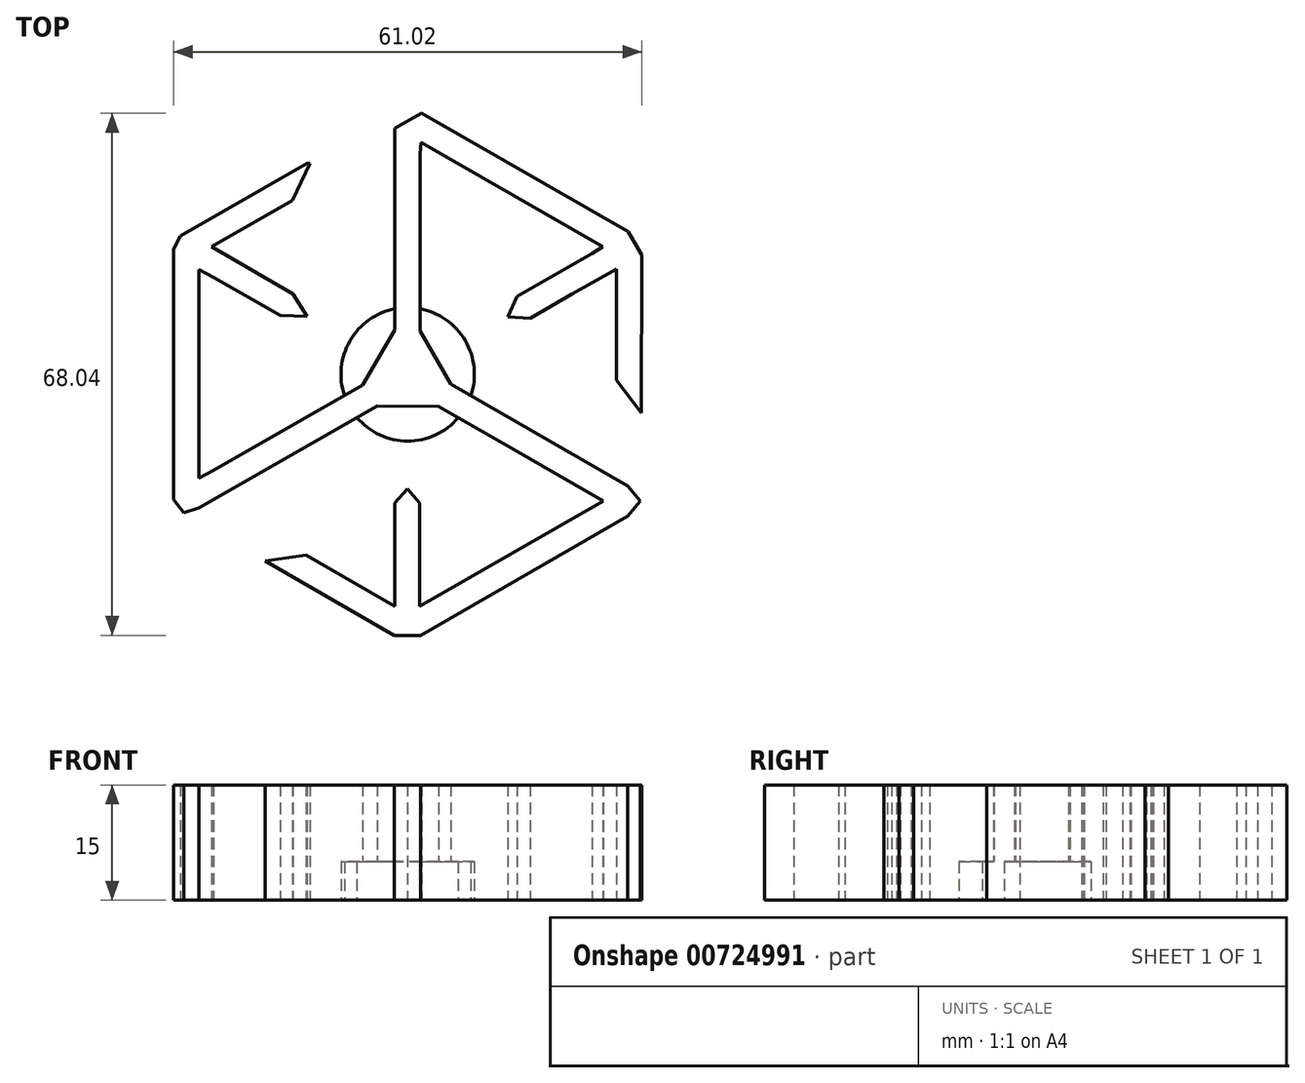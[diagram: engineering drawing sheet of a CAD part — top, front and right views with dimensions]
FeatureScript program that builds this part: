
annotation { "Feature Type Name" : "Feature", "Feature Type Description" : "" }
export const myFeature = defineFeature(function(context is Context, id is Id, definition is map)
    precondition{}
    {
        {
            var Q0;
            Q0=qCreatedBy(makeId("Top.planeOp"),FACE);
            var sketch = newSketch(context, id + "F0", { "sketchPlane" : qUnion([Q0])});
            skLineSegment(sketch, "E0", {"start": v(30.48, -5.05) * mm, "end": v(27.22, -0.75) * mm});
            skLineSegment(sketch, "E1", {"start": v(27.22, -0.75) * mm, "end": v(27.22, 13.73) * mm});
            skLineSegment(sketch, "E2", {"start": v(27.22, 13.73) * mm, "end": v(21.44, 10.46) * mm});
            skLineSegment(sketch, "E3", {"start": v(21.44, 10.46) * mm, "end": v(15.95, 7.3) * mm});
            skLineSegment(sketch, "E4", {"start": v(15.95, 7.3) * mm, "end": v(13.04, 7.5) * mm});
            skLineSegment(sketch, "E5", {"start": v(13.04, 7.5) * mm, "end": v(14.24, 10.14) * mm});
            skLineSegment(sketch, "E6", {"start": v(14.24, 10.14) * mm, "end": v(24.02, 15.76) * mm});
            skLineSegment(sketch, "E7", {"start": v(24.02, 15.76) * mm, "end": v(25.41, 16.65) * mm});
            skLineSegment(sketch, "E8", {"start": v(25.41, 16.65) * mm, "end": v(1.75, 30.23) * mm});
            skLineSegment(sketch, "E9", {"start": v(1.75, 30.23) * mm, "end": v(1.6, 28.74) * mm});
            skLineSegment(sketch, "E10", {"start": v(1.6, 28.74) * mm, "end": v(1.6, 5.63) * mm});
            skLineSegment(sketch, "E11", {"start": v(1.6, 5.63) * mm, "end": v(5.62, -1.29) * mm});
            skLineSegment(sketch, "E12", {"start": v(5.62, -1.29) * mm, "end": v(28.68, -14.56) * mm});
            skLineSegment(sketch, "E13", {"start": v(28.68, -14.56) * mm, "end": v(30.33, -16.5) * mm});
            skLineSegment(sketch, "E14", {"start": v(30.33, -16.5) * mm, "end": v(28.7, -18.47) * mm});
            skLineSegment(sketch, "E15", {"start": v(28.7, -18.47) * mm, "end": v(1.66, -34.02) * mm});
            skLineSegment(sketch, "E16", {"start": v(1.66, -34.02) * mm, "end": v(-1.74, -34.02) * mm});
            skLineSegment(sketch, "E17", {"start": v(-1.74, -34.02) * mm, "end": v(-18.56, -24.35) * mm});
            skLineSegment(sketch, "E18", {"start": v(-18.56, -24.35) * mm, "end": v(-13.27, -23.57) * mm});
            skLineSegment(sketch, "E19", {"start": v(-13.27, -23.57) * mm, "end": v(-1.67, -30.21) * mm});
            skLineSegment(sketch, "E20", {"start": v(-1.67, -30.21) * mm, "end": v(-1.67, -25.25) * mm});
            skLineSegment(sketch, "E21", {"start": v(-1.67, -25.25) * mm, "end": v(-1.66, -16.78) * mm});
            skLineSegment(sketch, "E22", {"start": v(-1.66, -16.78) * mm, "end": v(-0.03, -14.93) * mm});
            skLineSegment(sketch, "E23", {"start": v(-0.03, -14.93) * mm, "end": v(1.58, -16.8) * mm});
            skLineSegment(sketch, "E24", {"start": v(1.58, -16.8) * mm, "end": v(1.59, -27.9) * mm});
            skLineSegment(sketch, "E25", {"start": v(1.59, -27.9) * mm, "end": v(1.59, -30.21) * mm});
            skLineSegment(sketch, "E26", {"start": v(1.59, -30.21) * mm, "end": v(25.48, -16.52) * mm});
            skLineSegment(sketch, "E27", {"start": v(25.48, -16.52) * mm, "end": v(13.8, -9.78) * mm});
            skLineSegment(sketch, "E28", {"start": v(13.8, -9.78) * mm, "end": v(4.02, -4.18) * mm});
            skLineSegment(sketch, "E29", {"start": v(4.02, -4.18) * mm, "end": v(-3.99, -4.13) * mm});
            skLineSegment(sketch, "E30", {"start": v(-3.99, -4.13) * mm, "end": v(-27.24, -17.43) * mm});
            skLineSegment(sketch, "E31", {"start": v(-27.24, -17.43) * mm, "end": v(-29.15, -18.03) * mm});
            skLineSegment(sketch, "E32", {"start": v(-29.15, -18.03) * mm, "end": v(-30.49, -16.32) * mm});
            skLineSegment(sketch, "E33", {"start": v(-30.49, -16.32) * mm, "end": v(-30.51, 16.31) * mm});
            skLineSegment(sketch, "E34", {"start": v(-30.51, 16.31) * mm, "end": v(-29.6, 18.05) * mm});
            skLineSegment(sketch, "E35", {"start": v(-29.6, 18.05) * mm, "end": v(-13.09, 27.5) * mm});
            skLineSegment(sketch, "E36", {"start": v(-13.09, 27.5) * mm, "end": v(-12.76, 27.5) * mm});
            skLineSegment(sketch, "E37", {"start": v(-12.76, 27.5) * mm, "end": v(-15, 22.68) * mm});
            skLineSegment(sketch, "E38", {"start": v(-15, 22.68) * mm, "end": v(-25.55, 16.6) * mm});
            skLineSegment(sketch, "E39", {"start": v(-25.55, 16.6) * mm, "end": v(-14.95, 10.5) * mm});
            skLineSegment(sketch, "E40", {"start": v(-14.95, 10.5) * mm, "end": v(-13.14, 7.53) * mm});
            skLineSegment(sketch, "E41", {"start": v(-13.14, 7.53) * mm, "end": v(-16.62, 7.65) * mm});
            skLineSegment(sketch, "E42", {"start": v(-16.62, 7.65) * mm, "end": v(-25.34, 12.64) * mm});
            skLineSegment(sketch, "E43", {"start": v(-25.34, 12.64) * mm, "end": v(-27.19, 13.63) * mm});
            skLineSegment(sketch, "E44", {"start": v(-27.19, 13.63) * mm, "end": v(-27.19, -13.54) * mm});
            skLineSegment(sketch, "E45", {"start": v(-27.19, -13.54) * mm, "end": v(-25.28, -12.52) * mm});
            skLineSegment(sketch, "E46", {"start": v(-25.28, -12.52) * mm, "end": v(-5.85, -1.42) * mm});
            skLineSegment(sketch, "E47", {"start": v(-5.85, -1.42) * mm, "end": v(-1.66, 5.79) * mm});
            skLineSegment(sketch, "E48", {"start": v(-1.66, 5.79) * mm, "end": v(-1.66, 32.07) * mm});
            skLineSegment(sketch, "E49", {"start": v(-1.66, 32.07) * mm, "end": v(1.79, 34.02) * mm});
            skLineSegment(sketch, "E50", {"start": v(1.79, 34.02) * mm, "end": v(28.7, 18.62) * mm});
            skLineSegment(sketch, "E51", {"start": v(28.7, 18.62) * mm, "end": v(30.51, 15.56) * mm});
            skLineSegment(sketch, "E52", {"start": v(30.51, 15.56) * mm, "end": v(30.48, -5.05) * mm});
            skSolve(sketch);
        }
        {
            var Q0;
            Q0 = qSketchRegion(id + "F0", true);
            extrude(context, id + "F1", {"entities" : qUnion([Q0]), "depth" : 15 * mm, "offsetDistance" : 25 * mm});
        }
        {
            var Q0;
            Q0=qCreatedBy(makeId("Top.planeOp"),FACE);
            var sketch = newSketch(context, id + "F2", { "sketchPlane" : qUnion([Q0])});
            skCircle(sketch, "E53", {"center": v(0, 0) * mm, "radius": 8.7 * mm});
            skSolve(sketch);
        }
        {
            var Q0;
            Q0 = qSketchRegion(id + "F2", true);
            extrude(context, id + "F3", {"entities" : qUnion([Q0]), "operationType" : NewBodyOperationType.ADD, "depth" : 5 * mm, "offsetDistance" : 25 * mm});
        }
    });
